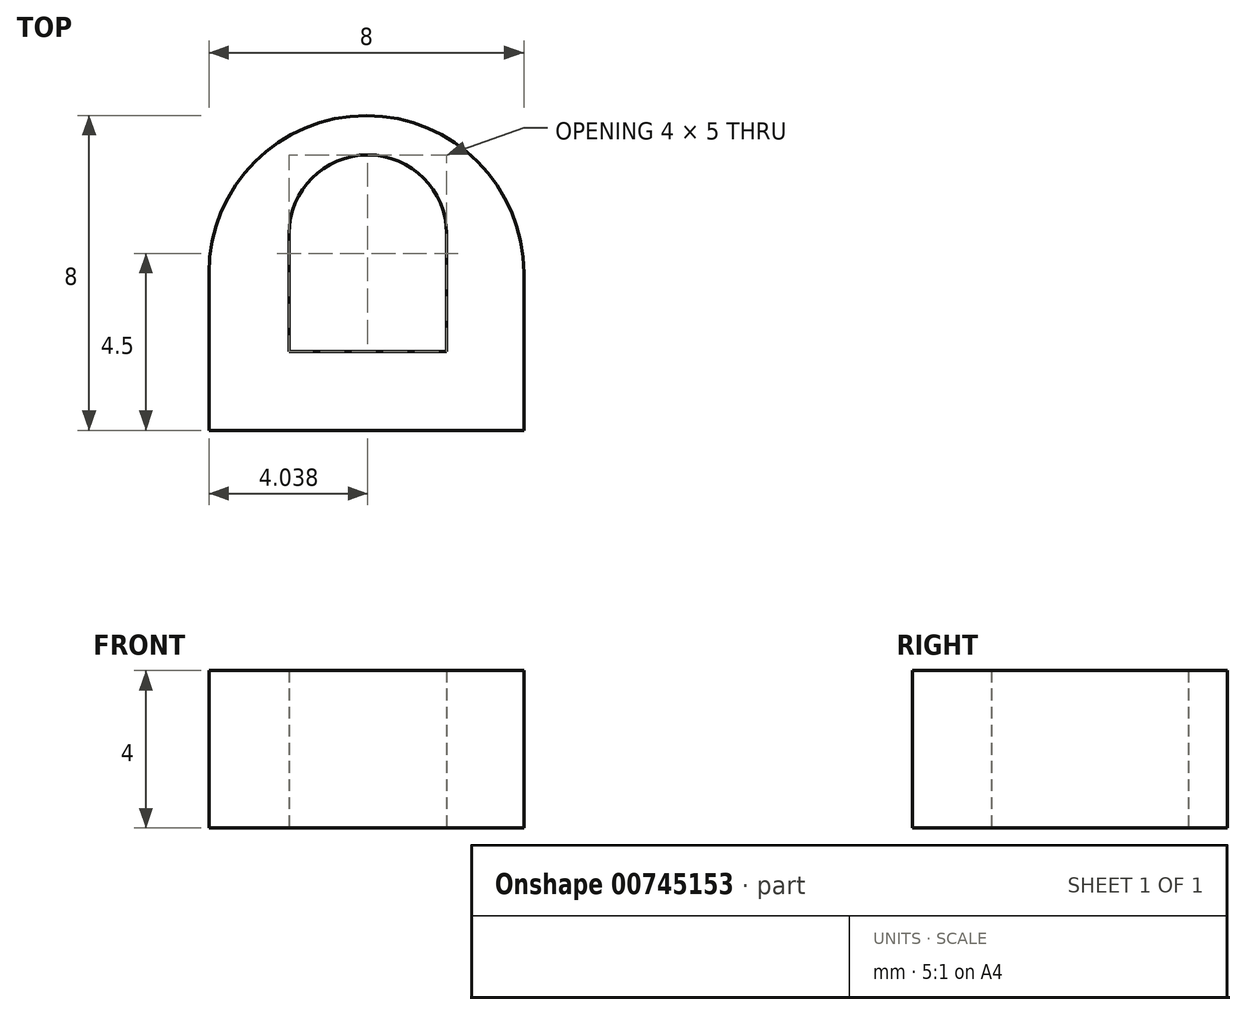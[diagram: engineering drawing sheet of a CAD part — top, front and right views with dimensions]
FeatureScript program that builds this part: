
annotation { "Feature Type Name" : "Feature", "Feature Type Description" : "" }
export const myFeature = defineFeature(function(context is Context, id is Id, definition is map)
    precondition{}
    {
        {
            var Q0;
            Q0=qCreatedBy(makeId("Top.planeOp"),FACE);
            var sketch = newSketch(context, id + "F0", { "sketchPlane" : qUnion([Q0])});
            skLineSegment(sketch, "E0.bottom", {"start": v(-4, 4) * mm, "end": v(4, 4) * mm});
            skLineSegment(sketch, "E0.top", {"start": v(-4, -4) * mm, "end": v(4, -4) * mm});
            skLineSegment(sketch, "E0.left", {"start": v(-4, 4) * mm, "end": v(-4, -4) * mm});
            skLineSegment(sketch, "E0.right", {"start": v(4, 4) * mm, "end": v(4, -4) * mm});
            skLineSegment(sketch, "E1", {"start": v(-1.96, 1) * mm, "end": v(-1.96, -2) * mm});
            skLineSegment(sketch, "E2", {"start": v(-1.96, -2) * mm, "end": v(2.04, -2) * mm});
            skLineSegment(sketch, "E3", {"start": v(2.04, -2) * mm, "end": v(2.04, 1) * mm});
            skArc(sketch, "E4", {"start": v(2.04, 1) * mm, "mid": v(0.04, 3) * mm, "end": v(-1.96, 1) * mm});
            skSolve(sketch);
        }
        {
            var Q0;
            Q0=makeQuery(id+"F0.imprint","IMPRINT",FACE,{"disambiguationData":[TD([[makeQuery(id+"F0.imprint","IMPRINT",EDGE,{"derivedFrom":sQuery(id+"F0.wireOp",EDGE,"E0.bottom")}),-1.0]])]});
            extrude(context, id + "F1", {"entities" : qUnion([Q0]), "depth" : 4 * mm, "offsetDistance" : 25 * mm});
        }
        {
            var Q0;
            Q0=makeQuery(id+"F1.opExtrude","SWEPT_EDGE",EDGE,{"disambiguationData":[OSD([sQuery(id+"F0.wireOp",EDGE,"E0.bottom"),sQuery(id+"F0.wireOp",EDGE,"E0.right")])]});
            fillet(context, id + "F2", {"entities" : qUnion([Q0]), "radius" : 4 * mm, "tangentPropagation" : true, "allowEdgeOverflow" : false});
        }
        {
            var Q0;
            Q0=makeQuery(id+"F1.opExtrude","SWEPT_EDGE",EDGE,{"disambiguationData":[OSD([sQuery(id+"F0.wireOp",EDGE,"E0.bottom"),sQuery(id+"F0.wireOp",EDGE,"E0.left")])]});
            fillet(context, id + "F3", {"entities" : qUnion([Q0]), "radius" : 4 * mm, "tangentPropagation" : true, "allowEdgeOverflow" : false});
        }
    });
